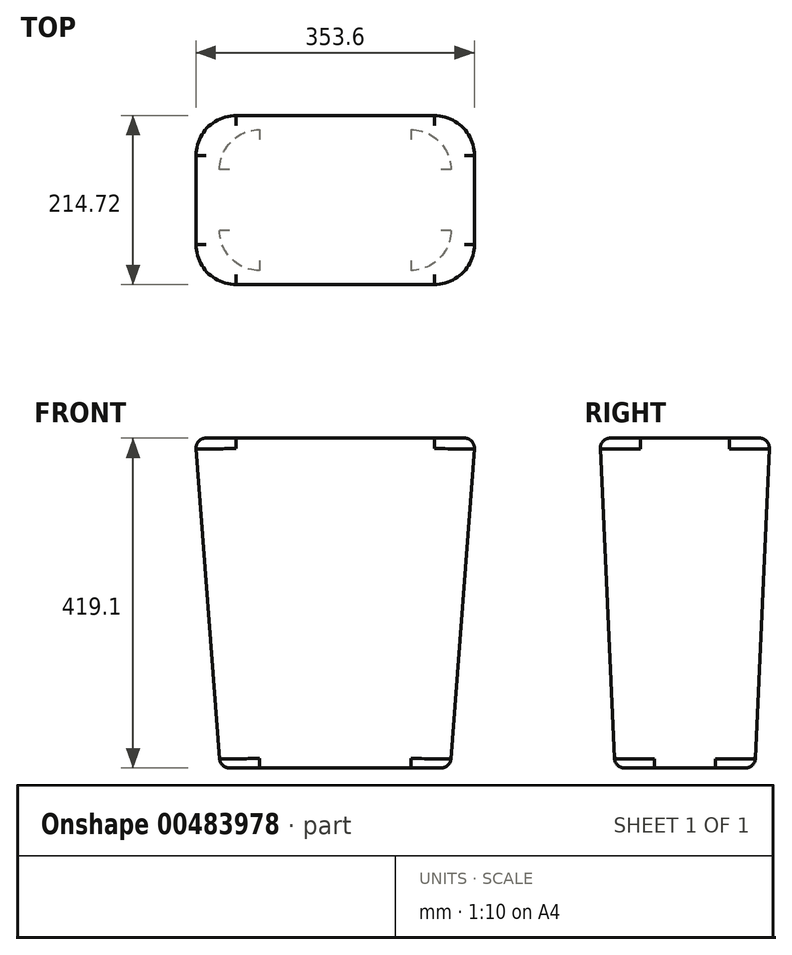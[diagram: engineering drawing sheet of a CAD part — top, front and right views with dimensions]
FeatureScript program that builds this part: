
annotation { "Feature Type Name" : "Feature", "Feature Type Description" : "" }
export const myFeature = defineFeature(function(context is Context, id is Id, definition is map)
    precondition{}
    {
        {
            var Q0;
            Q0=qCreatedBy(makeId("Top.planeOp"),FACE);
            var sketch = newSketch(context, id + "F0", { "sketchPlane" : qUnion([Q0])});
            skLineSegment(sketch, "E0.bottom", {"start": v(146.05, -88.9) * mm, "end": v(-146.05, -88.9) * mm});
            skLineSegment(sketch, "E0.top", {"start": v(146.05, 88.9) * mm, "end": v(-146.05, 88.9) * mm});
            skLineSegment(sketch, "E0.left", {"start": v(146.05, -88.9) * mm, "end": v(146.05, 88.9) * mm});
            skLineSegment(sketch, "E0.right", {"start": v(-146.05, -88.9) * mm, "end": v(-146.05, 88.9) * mm});
            skPoint(sketch, "E0.middle", {"position": v(0, 0) * mm});
            skSolve(sketch);
        }
        {
            var Q0;
            Q0=qCreatedBy(makeId("Top.planeOp"),FACE);
            cPlane(context, id + "F1", {"entities" : qUnion([Q0]), "cplaneType" : CPlaneType.OFFSET, "offset" : 419.1 * mm, "width" : 152.4 * mm, "height" : 152.4 * mm});
        }
        {
            var Q0;
            Q0=qCreatedBy(id+"F1.planeOp",FACE);
            var sketch = newSketch(context, id + "F2", { "sketchPlane" : qUnion([Q0])});
            skLineSegment(sketch, "E1.bottom", {"start": v(177.8, -107.95) * mm, "end": v(-177.8, -107.95) * mm});
            skLineSegment(sketch, "E1.top", {"start": v(177.8, 107.95) * mm, "end": v(-177.8, 107.95) * mm});
            skLineSegment(sketch, "E1.left", {"start": v(177.8, -107.95) * mm, "end": v(177.8, 107.95) * mm});
            skLineSegment(sketch, "E1.right", {"start": v(-177.8, -107.95) * mm, "end": v(-177.8, 107.95) * mm});
            skPoint(sketch, "E1.middle", {"position": v(0, 0) * mm});
            skSolve(sketch);
        }
        {
            var Q0;
            Q0 = qSketchRegion(id + "F0", true);
            var Q1;
            Q1 = qSketchRegion(id + "F2", true);
            loft(context, id + "F3", {"sheetProfilesArray" : [{ "sheetProfileEntities" : qUnion([Q0]) }, { "sheetProfileEntities" : qUnion([Q1]) }]});
        }
        {
            var Q0;
            Q0=makeQuery(id+"F3.opLoft","SWEPT_EDGE",EDGE,{"disambiguationData":[OSD([sQuery(id+"F0.wireOp",EDGE,"E0.bottom"),sQuery(id+"F0.wireOp",EDGE,"E0.right"),sQuery(id+"F2.wireOp",EDGE,"E1.bottom"),sQuery(id+"F2.wireOp",EDGE,"E1.right")])]});
            var Q1;
            Q1=makeQuery(id+"F3.opLoft","SWEPT_EDGE",EDGE,{"disambiguationData":[OSD([sQuery(id+"F0.wireOp",EDGE,"E0.bottom"),sQuery(id+"F0.wireOp",EDGE,"E0.left"),sQuery(id+"F2.wireOp",EDGE,"E1.bottom"),sQuery(id+"F2.wireOp",EDGE,"E1.left")])]});
            var Q2;
            Q2=makeQuery(id+"F3.opLoft","SWEPT_EDGE",EDGE,{"disambiguationData":[OSD([sQuery(id+"F0.wireOp",EDGE,"E0.top"),sQuery(id+"F0.wireOp",EDGE,"E0.left"),sQuery(id+"F2.wireOp",EDGE,"E1.top"),sQuery(id+"F2.wireOp",EDGE,"E1.left")])]});
            var Q3;
            Q3=makeQuery(id+"F3.opLoft","SWEPT_EDGE",EDGE,{"disambiguationData":[OSD([sQuery(id+"F0.wireOp",EDGE,"E0.top"),sQuery(id+"F0.wireOp",EDGE,"E0.right"),sQuery(id+"F2.wireOp",EDGE,"E1.top"),sQuery(id+"F2.wireOp",EDGE,"E1.right")])]});
            fillet(context, id + "F4", {"entities" : qUnion([Q0, Q1, Q2, Q3]), "radius" : 50.8 * mm, "tangentPropagation" : true, "allowEdgeOverflow" : false});
        }
        {
            var Q0;
            Q0=makeQuery(id+"F3.opLoft","MID_CAP_EDGE",EDGE,{"disambiguationData":[OSD([sQuery(id+"F2.wireOp",EDGE,"E1.bottom"),sQuery(id+"F2.wireOp",EDGE,"E1.top"),sQuery(id+"F2.wireOp",EDGE,"E1.right")])],"capPos":1.0});
            var Q1;
            Q1=makeQuery(id+"F3.opLoft","MID_CAP_EDGE",EDGE,{"disambiguationData":[OSD([sQuery(id+"F0.wireOp",EDGE,"E0.bottom"),sQuery(id+"F0.wireOp",EDGE,"E0.top"),sQuery(id+"F0.wireOp",EDGE,"E0.right")])],"capPos":0.0});
            fillet(context, id + "F5", {"entities" : qUnion([Q0, Q1]), "radius" : 12.7 * mm, "tangentPropagation" : true, "allowEdgeOverflow" : false});
        }
    });
